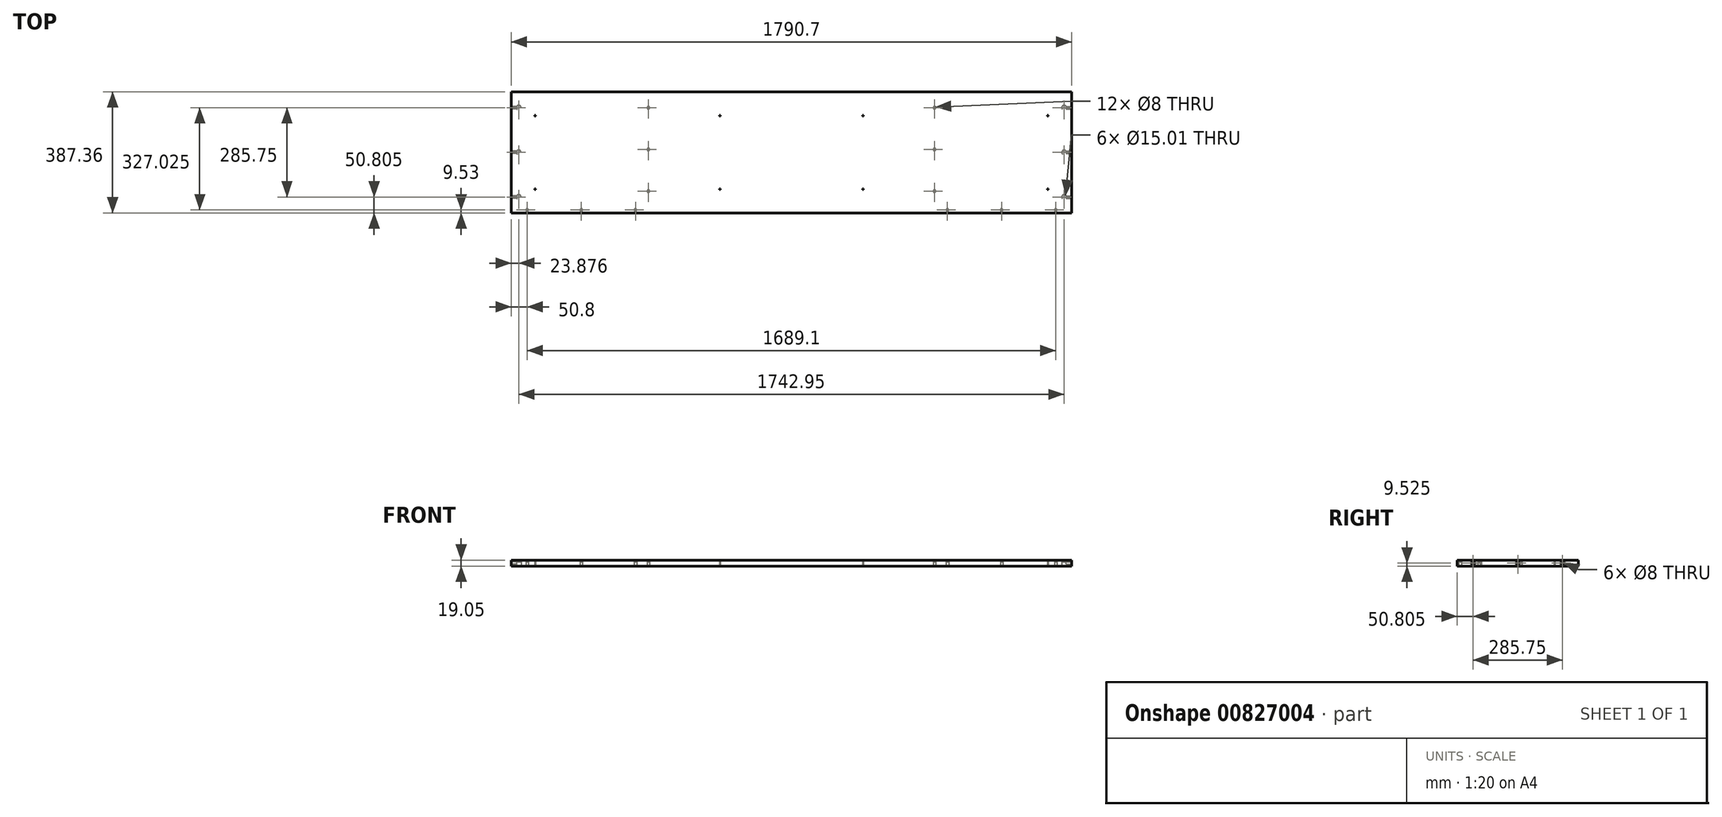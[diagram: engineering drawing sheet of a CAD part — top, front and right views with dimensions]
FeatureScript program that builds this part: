
annotation { "Feature Type Name" : "Feature", "Feature Type Description" : "" }
export const myFeature = defineFeature(function(context is Context, id is Id, definition is map)
    precondition{}
    {
        {
            var Q0;
            Q0=qCreatedBy(makeId("Top.planeOp"),FACE);
            var sketch = newSketch(context, id + "F0", { "sketchPlane" : qUnion([Q0])});
            skLineSegment(sketch, "E0.bottom", {"start": v(895.35, 193.67) * mm, "end": v(-895.35, 193.67) * mm});
            skLineSegment(sketch, "E0.top", {"start": v(895.35, -193.68) * mm, "end": v(-895.35, -193.68) * mm});
            skLineSegment(sketch, "E0.left", {"start": v(895.35, 193.67) * mm, "end": v(895.35, -193.68) * mm});
            skLineSegment(sketch, "E0.right", {"start": v(-895.35, 193.67) * mm, "end": v(-895.35, -193.68) * mm});
            skPoint(sketch, "E0.middle", {"position": v(0, 0) * mm});
            skSolve(sketch);
        }
        {
            var Q0;
            Q0=makeQuery(id+"F0.imprint","IMPRINT",FACE,{"disambiguationData":[TD([[makeQuery(id+"F0.imprint","IMPRINT",EDGE,{"derivedFrom":sQuery(id+"F0.wireOp",EDGE,"E0.bottom")}),1.0]])]});
            extrude(context, id + "F1", {"entities" : qUnion([Q0]), "depth" : 19.05 * mm, "offsetDistance" : 25.4 * mm});
        }
        {
            var Q0;
            Q0=makeQuery(id+"F1.opExtrude","CAP_FACE",FACE,{"disambiguationData":[OSD([sQuery(id+"F0.wireOp",EDGE,"E0.bottom"),sQuery(id+"F0.wireOp",EDGE,"E0.top"),sQuery(id+"F0.wireOp",EDGE,"E0.left"),sQuery(id+"F0.wireOp",EDGE,"E0.right")])],"isStart":true});
            var sketch = newSketch(context, id + "F2", { "sketchPlane" : qUnion([Q0])});
            skLineSegment(sketch, "E1", {"start": v(-895.35, -193.67) * mm, "end": v(-457.15, -193.67) * mm});
            skLineSegment(sketch, "E2", {"start": v(895.35, -193.67) * mm, "end": v(457.15, -193.67) * mm});
            skLineSegment(sketch, "E3", {"start": v(-457.15, -193.67) * mm, "end": v(-466.67, -193.67) * mm});
            skLineSegment(sketch, "E4", {"start": v(457.15, -193.67) * mm, "end": v(466.67, -193.67) * mm});
            skLineSegment(sketch, "E5.bottom", {"start": v(-466.67, -193.67) * mm, "end": v(-447.62, -193.67) * mm});
            skLineSegment(sketch, "E5.top", {"start": v(-466.67, 174.63) * mm, "end": v(-447.62, 174.63) * mm});
            skLineSegment(sketch, "E5.left", {"start": v(-466.67, -193.67) * mm, "end": v(-466.67, 174.62) * mm});
            skLineSegment(sketch, "E5.right", {"start": v(-447.62, -193.67) * mm, "end": v(-447.62, 174.62) * mm});
            skLineSegment(sketch, "E6.bottom", {"start": v(466.67, -193.67) * mm, "end": v(447.62, -193.67) * mm});
            skLineSegment(sketch, "E6.top", {"start": v(466.67, 174.63) * mm, "end": v(447.62, 174.63) * mm});
            skLineSegment(sketch, "E6.left", {"start": v(466.67, -193.67) * mm, "end": v(466.67, 174.63) * mm});
            skLineSegment(sketch, "E6.right", {"start": v(447.62, -193.67) * mm, "end": v(447.62, 174.63) * mm});
            skLineSegment(sketch, "E7", {"start": v(-457.15, 174.63) * mm, "end": v(-457.15, 123.83) * mm});
            skLineSegment(sketch, "E8", {"start": v(-457.15, -193.67) * mm, "end": v(-457.15, -142.87) * mm});
            skLineSegment(sketch, "E9", {"start": v(457.15, 174.63) * mm, "end": v(457.15, 123.83) * mm});
            skLineSegment(sketch, "E10", {"start": v(457.15, -193.68) * mm, "end": v(457.15, -142.87) * mm});
            skLineSegment(sketch, "E11", {"start": v(-466.67, -9.52) * mm, "end": v(-447.62, -9.52) * mm});
            skLineSegment(sketch, "E12", {"start": v(466.67, -9.52) * mm, "end": v(447.62, -9.52) * mm});
            skPoint(sketch, "E13", {"position": v(-457.15, -9.52) * mm});
            skPoint(sketch, "E14", {"position": v(-457.15, -142.87) * mm});
            skPoint(sketch, "E15", {"position": v(-457.15, 123.83) * mm});
            skPoint(sketch, "E16", {"position": v(457.15, 123.83) * mm});
            skPoint(sketch, "E17", {"position": v(457.15, -142.87) * mm});
            skPoint(sketch, "E18", {"position": v(457.15, -9.52) * mm});
            skLineSegment(sketch, "E19.bottom", {"start": v(-447.62, 174.63) * mm, "end": v(-895.35, 174.63) * mm});
            skLineSegment(sketch, "E19.top", {"start": v(-447.62, 193.68) * mm, "end": v(-895.35, 193.68) * mm});
            skLineSegment(sketch, "E19.left", {"start": v(-447.62, 174.62) * mm, "end": v(-447.62, 193.68) * mm});
            skLineSegment(sketch, "E19.right", {"start": v(-895.35, 174.63) * mm, "end": v(-895.35, 193.68) * mm});
            skLineSegment(sketch, "E20.bottom", {"start": v(447.62, 174.63) * mm, "end": v(895.35, 174.63) * mm});
            skLineSegment(sketch, "E20.top", {"start": v(447.62, 193.68) * mm, "end": v(895.35, 193.68) * mm});
            skLineSegment(sketch, "E20.left", {"start": v(447.62, 174.63) * mm, "end": v(447.62, 193.67) * mm});
            skLineSegment(sketch, "E20.right", {"start": v(895.35, 174.63) * mm, "end": v(895.35, 193.68) * mm});
            skLineSegment(sketch, "E21", {"start": v(-447.62, 184.15) * mm, "end": v(-498.42, 184.15) * mm});
            skLineSegment(sketch, "E22", {"start": v(-895.35, 184.15) * mm, "end": v(-844.55, 184.15) * mm});
            skLineSegment(sketch, "E23", {"start": v(-671.49, 174.63) * mm, "end": v(-671.49, 193.68) * mm});
            skLineSegment(sketch, "E24", {"start": v(447.62, 184.15) * mm, "end": v(498.42, 184.15) * mm});
            skLineSegment(sketch, "E25", {"start": v(895.35, 184.15) * mm, "end": v(844.55, 184.15) * mm});
            skLineSegment(sketch, "E26", {"start": v(498.42, 184.15) * mm, "end": v(844.55, 184.15) * mm});
            skPoint(sketch, "E27", {"position": v(671.49, 184.15) * mm});
            skPoint(sketch, "E28", {"position": v(844.55, 184.15) * mm});
            skPoint(sketch, "E29", {"position": v(498.42, 184.15) * mm});
            skPoint(sketch, "E30", {"position": v(-844.55, 184.15) * mm});
            skPoint(sketch, "E31", {"position": v(-671.49, 184.15) * mm});
            skPoint(sketch, "E32", {"position": v(-498.42, 184.15) * mm});
            skSolve(sketch);
        }
        {
            var Q0;
            Q0=sQuery(id+"F2.wireOp",VERTEX,"E30");
            var Q1;
            Q1=sQuery(id+"F2.wireOp",VERTEX,"E31");
            var Q2;
            Q2=sQuery(id+"F2.wireOp",VERTEX,"E32");
            var Q3;
            Q3=sQuery(id+"F2.wireOp",VERTEX,"E15");
            var Q4;
            Q4=sQuery(id+"F2.wireOp",VERTEX,"E13");
            var Q5;
            Q5=sQuery(id+"F2.wireOp",VERTEX,"E14");
            var Q6;
            Q6=sQuery(id+"F2.wireOp",VERTEX,"E17");
            var Q7;
            Q7=sQuery(id+"F2.wireOp",VERTEX,"E18");
            var Q8;
            Q8=sQuery(id+"F2.wireOp",VERTEX,"E16");
            var Q9;
            Q9=sQuery(id+"F2.wireOp",VERTEX,"E29");
            var Q10;
            Q10=sQuery(id+"F2.wireOp",VERTEX,"E27");
            var Q11;
            Q11=sQuery(id+"F2.wireOp",VERTEX,"E28");
            var Q12;
            Q12=makeQuery(id+"F1.opExtrude","SWEPT_BODY",BODY,{"disambiguationData":[OSD([sQuery(id+"F0.wireOp",EDGE,"E0.bottom"),sQuery(id+"F0.wireOp",EDGE,"E0.top"),sQuery(id+"F0.wireOp",EDGE,"E0.left"),sQuery(id+"F0.wireOp",EDGE,"E0.right")])]});
            hole(context, id + "F3", {"style" : HoleStyle.SIMPLE, "endStyle" : HoleEndStyle.BLIND, "holeDiameter" : 8 * mm, "majorDiameter" : 6.35 * mm, "holeDepth" : 14.22 * mm, "isTappedThrough" : true, "tappedDepth" : 12.7 * mm, "tapClearance" : 3, "startFromSketch" : true, "locations" : qUnion([Q0, Q1, Q2, Q3, Q4, Q5, Q6, Q7, Q8, Q9, Q10, Q11]), "scope" : qUnion([Q12])});
        }
        {
            var Q0;
            Q0=makeQuery(id+"F1.opExtrude","CAP_FACE",FACE,{"disambiguationData":[OSD([sQuery(id+"F0.wireOp",EDGE,"E0.bottom"),sQuery(id+"F0.wireOp",EDGE,"E0.top"),sQuery(id+"F0.wireOp",EDGE,"E0.left"),sQuery(id+"F0.wireOp",EDGE,"E0.right")])],"isStart":true});
            var sketch = newSketch(context, id + "F4", { "sketchPlane" : qUnion([Q0])});
            skLineSegment(sketch, "E33", {"start": v(-895.35, 193.68) * mm, "end": v(-871.47, 193.68) * mm});
            skLineSegment(sketch, "E34", {"start": v(-871.47, 193.68) * mm, "end": v(-871.47, 142.88) * mm});
            skLineSegment(sketch, "E35", {"start": v(-895.35, -193.67) * mm, "end": v(-871.47, -193.67) * mm});
            skLineSegment(sketch, "E36", {"start": v(-871.47, -193.67) * mm, "end": v(-871.47, -142.88) * mm});
            skLineSegment(sketch, "E37", {"start": v(-895.35, 0) * mm, "end": v(-871.47, 0) * mm});
            skLineSegment(sketch, "E38", {"start": v(895.35, 193.68) * mm, "end": v(871.47, 193.68) * mm});
            skLineSegment(sketch, "E39", {"start": v(871.47, 193.68) * mm, "end": v(871.47, 142.88) * mm});
            skLineSegment(sketch, "E40", {"start": v(895.35, -193.67) * mm, "end": v(871.47, -193.67) * mm});
            skLineSegment(sketch, "E41", {"start": v(871.47, -193.67) * mm, "end": v(871.47, -142.87) * mm});
            skLineSegment(sketch, "E42", {"start": v(895.35, 0) * mm, "end": v(871.47, 0) * mm});
            skPoint(sketch, "E43", {"position": v(-871.47, 142.88) * mm});
            skPoint(sketch, "E44", {"position": v(-871.47, 0) * mm});
            skPoint(sketch, "E45", {"position": v(-871.47, -142.88) * mm});
            skPoint(sketch, "E46", {"position": v(871.47, 142.88) * mm});
            skPoint(sketch, "E47", {"position": v(871.47, 0) * mm});
            skPoint(sketch, "E48", {"position": v(871.47, -142.87) * mm});
            skSolve(sketch);
        }
        {
            var Q0;
            Q0=sQuery(id+"F4.wireOp",VERTEX,"E43");
            var Q1;
            Q1=sQuery(id+"F4.wireOp",VERTEX,"E44");
            var Q2;
            Q2=sQuery(id+"F4.wireOp",VERTEX,"E45");
            var Q3;
            Q3=sQuery(id+"F4.wireOp",VERTEX,"E46");
            var Q4;
            Q4=sQuery(id+"F4.wireOp",VERTEX,"E47");
            var Q5;
            Q5=sQuery(id+"F4.wireOp",VERTEX,"E48");
            var Q6;
            Q6=makeQuery(id+"F1.opExtrude","SWEPT_BODY",BODY,{"disambiguationData":[OSD([sQuery(id+"F0.wireOp",EDGE,"E0.bottom"),sQuery(id+"F0.wireOp",EDGE,"E0.top"),sQuery(id+"F0.wireOp",EDGE,"E0.left"),sQuery(id+"F0.wireOp",EDGE,"E0.right")])]});
            hole(context, id + "F5", {"style" : HoleStyle.SIMPLE, "endStyle" : HoleEndStyle.BLIND, "holeDiameter" : 15 * mm, "majorDiameter" : 6.35 * mm, "holeDepth" : 14.22 * mm, "isTappedThrough" : true, "tappedDepth" : 12.7 * mm, "tapClearance" : 3, "startFromSketch" : true, "locations" : qUnion([Q0, Q1, Q2, Q3, Q4, Q5]), "scope" : qUnion([Q6])});
        }
        {
            var Q0;
            Q0=makeQuery(id+"F1.opExtrude","CAP_FACE",FACE,{"disambiguationData":[OSD([sQuery(id+"F0.wireOp",EDGE,"E0.bottom"),sQuery(id+"F0.wireOp",EDGE,"E0.top"),sQuery(id+"F0.wireOp",EDGE,"E0.left"),sQuery(id+"F0.wireOp",EDGE,"E0.right")])],"isStart":true});
            var sketch = newSketch(context, id + "F6", { "sketchPlane" : qUnion([Q0])});
            skLineSegment(sketch, "E49.bottom", {"start": v(-895.35, 193.68) * mm, "end": v(-819.15, 193.68) * mm});
            skLineSegment(sketch, "E49.top", {"start": v(-895.35, 117.48) * mm, "end": v(-819.15, 117.48) * mm});
            skLineSegment(sketch, "E49.left", {"start": v(-895.35, 193.68) * mm, "end": v(-895.35, 117.48) * mm});
            skLineSegment(sketch, "E49.right", {"start": v(-819.15, 193.68) * mm, "end": v(-819.15, 117.48) * mm});
            skLineSegment(sketch, "E50.bottom", {"start": v(-895.35, -193.67) * mm, "end": v(-819.15, -193.67) * mm});
            skLineSegment(sketch, "E50.top", {"start": v(-895.35, -117.47) * mm, "end": v(-819.15, -117.47) * mm});
            skLineSegment(sketch, "E50.left", {"start": v(-895.35, -193.67) * mm, "end": v(-895.35, -117.47) * mm});
            skLineSegment(sketch, "E50.right", {"start": v(-819.15, -193.67) * mm, "end": v(-819.15, -117.47) * mm});
            skLineSegment(sketch, "E51.bottom", {"start": v(895.35, 193.68) * mm, "end": v(819.15, 193.68) * mm});
            skLineSegment(sketch, "E51.top", {"start": v(895.35, 117.48) * mm, "end": v(819.15, 117.48) * mm});
            skLineSegment(sketch, "E51.left", {"start": v(895.35, 193.68) * mm, "end": v(895.35, 117.48) * mm});
            skLineSegment(sketch, "E51.right", {"start": v(819.15, 193.68) * mm, "end": v(819.15, 117.48) * mm});
            skLineSegment(sketch, "E52.bottom", {"start": v(895.35, -193.67) * mm, "end": v(819.15, -193.67) * mm});
            skLineSegment(sketch, "E52.top", {"start": v(895.35, -117.47) * mm, "end": v(819.15, -117.47) * mm});
            skLineSegment(sketch, "E52.left", {"start": v(895.35, -193.67) * mm, "end": v(895.35, -117.47) * mm});
            skLineSegment(sketch, "E52.right", {"start": v(819.15, -193.67) * mm, "end": v(819.15, -117.47) * mm});
            skLineSegment(sketch, "E53.bottom", {"start": v(228.6, 117.48) * mm, "end": v(-228.6, 117.48) * mm});
            skLineSegment(sketch, "E53.top", {"start": v(228.6, -117.48) * mm, "end": v(-228.6, -117.48) * mm});
            skLineSegment(sketch, "E53.left", {"start": v(228.6, 117.48) * mm, "end": v(228.6, -117.48) * mm});
            skLineSegment(sketch, "E53.right", {"start": v(-228.6, 117.48) * mm, "end": v(-228.6, -117.48) * mm});
            skPoint(sketch, "E53.middle", {"position": v(0, 0) * mm});
            skSolve(sketch);
        }
        {
            var Q0;
            Q0=sQuery(id+"F6.wireOp",VERTEX,"E49.top.end");
            var Q1;
            Q1=sQuery(id+"F6.wireOp",VERTEX,"E50.top.end");
            var Q2;
            Q2=sQuery(id+"F6.wireOp",VERTEX,"E53.bottom.end");
            var Q3;
            Q3=sQuery(id+"F6.wireOp",VERTEX,"E53.top.end");
            var Q4;
            Q4=sQuery(id+"F6.wireOp",VERTEX,"E53.bottom.start");
            var Q5;
            Q5=sQuery(id+"F6.wireOp",VERTEX,"E51.top.end");
            var Q6;
            Q6=sQuery(id+"F6.wireOp",VERTEX,"E52.top.end");
            var Q7;
            Q7=sQuery(id+"F6.wireOp",VERTEX,"E53.top.start");
            var Q8;
            Q8=makeQuery(id+"F1.opExtrude","SWEPT_BODY",BODY,{"disambiguationData":[OSD([sQuery(id+"F0.wireOp",EDGE,"E0.bottom"),sQuery(id+"F0.wireOp",EDGE,"E0.top"),sQuery(id+"F0.wireOp",EDGE,"E0.left"),sQuery(id+"F0.wireOp",EDGE,"E0.right")])]});
            hole(context, id + "F7", {"style" : HoleStyle.SIMPLE, "endStyle" : HoleEndStyle.BLIND, "holeDiameter" : 3.17 * mm, "majorDiameter" : 6.35 * mm, "holeDepth" : 25.4 * mm, "isTappedThrough" : true, "tappedDepth" : 12.7 * mm, "tapClearance" : 3, "startFromSketch" : true, "locations" : qUnion([Q0, Q1, Q2, Q3, Q4, Q5, Q6, Q7]), "scope" : qUnion([Q8])});
        }
        {
            var Q0;
            Q0=makeQuery(id+"F1.opExtrude","SWEPT_FACE",FACE,{"disambiguationData":[OSD([sQuery(id+"F0.wireOp",EDGE,"E0.left")])]});
            var sketch = newSketch(context, id + "F8", { "sketchPlane" : qUnion([Q0])});
            skLineSegment(sketch, "E54", {"start": v(-193.67, 9.53) * mm, "end": v(-142.87, 9.53) * mm});
            skLineSegment(sketch, "E55", {"start": v(193.68, 9.53) * mm, "end": v(142.88, 9.53) * mm});
            skLineSegment(sketch, "E56", {"start": v(0, 0) * mm, "end": v(0, 19.05) * mm});
            skPoint(sketch, "E57", {"position": v(0, 9.53) * mm});
            skSolve(sketch);
        }
        {
            var Q0;
            Q0=sQuery(id+"F8.wireOp",VERTEX,"E54.end");
            var Q1;
            Q1=sQuery(id+"F8.wireOp",VERTEX,"E55.end");
            var Q2;
            Q2=sQuery(id+"F8.wireOp",VERTEX,"E57");
            var Q3;
            Q3=makeQuery(id+"F1.opExtrude","SWEPT_BODY",BODY,{"disambiguationData":[OSD([sQuery(id+"F0.wireOp",EDGE,"E0.bottom"),sQuery(id+"F0.wireOp",EDGE,"E0.top"),sQuery(id+"F0.wireOp",EDGE,"E0.left"),sQuery(id+"F0.wireOp",EDGE,"E0.right")])]});
            hole(context, id + "F9", {"style" : HoleStyle.SIMPLE, "endStyle" : HoleEndStyle.BLIND, "holeDiameter" : 8 * mm, "majorDiameter" : 6.35 * mm, "holeDepth" : 25.4 * mm, "isTappedThrough" : true, "tappedDepth" : 12.7 * mm, "tapClearance" : 3, "startFromSketch" : true, "locations" : qUnion([Q0, Q1, Q2]), "scope" : qUnion([Q3])});
        }
        {
            var Q0;
            Q0=makeQuery(id+"F1.opExtrude","SWEPT_FACE",FACE,{"disambiguationData":[OSD([sQuery(id+"F0.wireOp",EDGE,"E0.right")])]});
            var sketch = newSketch(context, id + "F10", { "sketchPlane" : qUnion([Q0])});
            skLineSegment(sketch, "E58", {"start": v(-193.67, 9.53) * mm, "end": v(-142.87, 9.53) * mm});
            skLineSegment(sketch, "E59", {"start": v(193.68, 9.53) * mm, "end": v(142.88, 9.53) * mm});
            skLineSegment(sketch, "E60", {"start": v(0, 0) * mm, "end": v(0, 9.53) * mm});
            skPoint(sketch, "E61", {"position": v(0, 9.53) * mm});
            skSolve(sketch);
        }
        {
            var Q0;
            Q0=sQuery(id+"F10.wireOp",VERTEX,"E58.end");
            var Q1;
            Q1=sQuery(id+"F10.wireOp",VERTEX,"E61");
            var Q2;
            Q2=sQuery(id+"F10.wireOp",VERTEX,"E59.end");
            var Q3;
            Q3=makeQuery(id+"F1.opExtrude","SWEPT_BODY",BODY,{"disambiguationData":[OSD([sQuery(id+"F0.wireOp",EDGE,"E0.bottom"),sQuery(id+"F0.wireOp",EDGE,"E0.top"),sQuery(id+"F0.wireOp",EDGE,"E0.left"),sQuery(id+"F0.wireOp",EDGE,"E0.right")])]});
            hole(context, id + "F11", {"style" : HoleStyle.SIMPLE, "endStyle" : HoleEndStyle.BLIND, "holeDiameter" : 8 * mm, "majorDiameter" : 6.35 * mm, "holeDepth" : 25.4 * mm, "isTappedThrough" : true, "tappedDepth" : 12.7 * mm, "tapClearance" : 3, "startFromSketch" : true, "locations" : qUnion([Q0, Q1, Q2]), "scope" : qUnion([Q3])});
        }
    });
